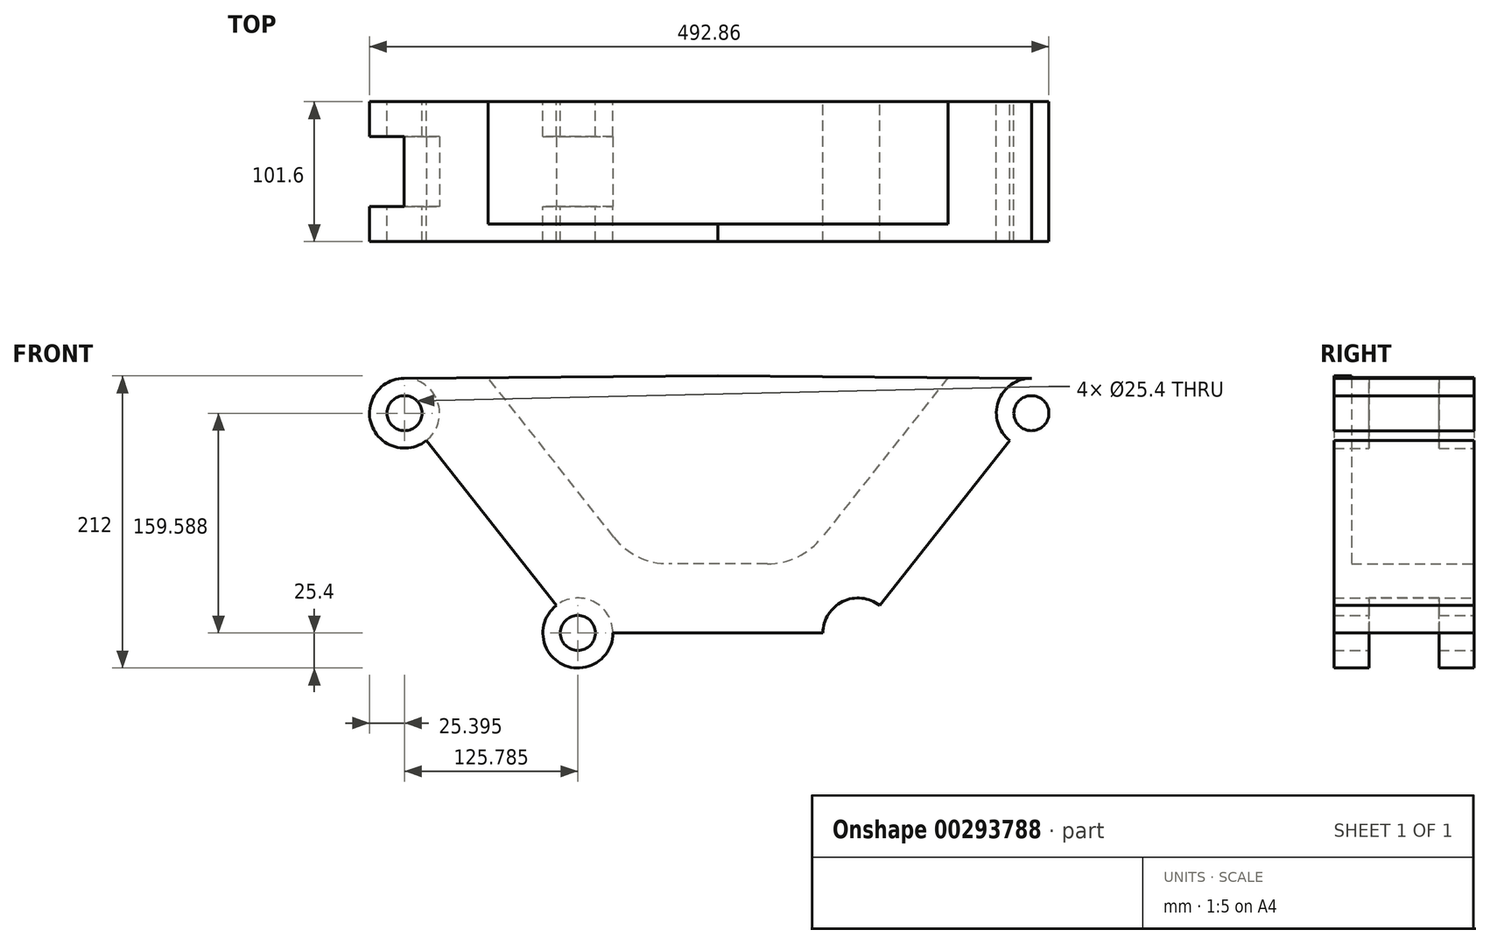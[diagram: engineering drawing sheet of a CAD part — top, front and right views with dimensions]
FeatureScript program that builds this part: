
annotation { "Feature Type Name" : "Feature", "Feature Type Description" : "" }
export const myFeature = defineFeature(function(context is Context, id is Id, definition is map)
    precondition{}
    {
        {
            var Q0;
            Q0=qCreatedBy(makeId("Front.planeOp"),FACE);
            var sketch = newSketch(context, id + "F0", { "sketchPlane" : qUnion([Q0])});
            skLineSegment(sketch, "E0", {"start": v(0, 0) * mm, "end": v(0, 76.2) * mm, "construction": true});
            skLineSegment(sketch, "E1", {"start": v(0, 0) * mm, "end": v(-101.6, 0) * mm});
            skLineSegment(sketch, "E2", {"start": v(-101.6, 0) * mm, "end": v(-227.38, 159.59) * mm});
            skCircle(sketch, "E3", {"center": v(-101.6, 0) * mm, "radius": 12.7 * mm});
            skCircle(sketch, "E4", {"center": v(-101.6, 0) * mm, "radius": 25.4 * mm});
            skCircle(sketch, "E5", {"center": v(-227.38, 159.59) * mm, "radius": 12.7 * mm});
            skCircle(sketch, "E6", {"center": v(-227.38, 159.59) * mm, "radius": 25.4 * mm});
            skLineSegment(sketch, "E7", {"start": v(-227.56, 184.99) * mm, "end": v(0, 186.6) * mm});
            skLineSegment(sketch, "E8.MirrorCS", {"start": v(227.56, 184.99) * mm, "end": v(0, 186.6) * mm});
            skCircle(sketch, "E9.MirrorC", {"center": v(227.38, 159.59) * mm, "radius": 25.4 * mm});
            skCircle(sketch, "E10.MirrorC", {"center": v(227.38, 159.59) * mm, "radius": 12.7 * mm});
            skCircle(sketch, "E11.MirrorC", {"center": v(101.6, 0) * mm, "radius": 25.4 * mm});
            skCircle(sketch, "E12.MirrorC", {"center": v(101.6, 0) * mm, "radius": 12.7 * mm});
            skLineSegment(sketch, "E13.MirrorCS", {"start": v(101.6, 0) * mm, "end": v(227.38, 159.59) * mm});
            skLineSegment(sketch, "E14.MirrorCS", {"start": v(0, 0) * mm, "end": v(101.6, 0) * mm});
            skSolve(sketch);
        }
        {
            var Q0;
            {var subQ0=sQuery(id+"F0.wireOp",EDGE,"E7");Q0=makeQuery(id+"F0.imprint","IMPRINT",FACE,{"disambiguationData":[TD([[makeQuery(id+"F0.imprint","IMPRINT",EDGE,{"derivedFrom":subQ0}),-1.0]])]});}
            cPlane(context, id + "F1", {"entities" : qUnion([Q0]), "cplaneType" : CPlaneType.OFFSET, "offset" : 101.6 * mm, "width" : 152.4 * mm, "height" : 152.4 * mm});
        }
        {
            var Q0;
            {var subQ0=sQuery(id+"F0.wireOp",EDGE,"E7");Q0=makeQuery(id+"F0.imprint","IMPRINT",FACE,{"disambiguationData":[TD([[makeQuery(id+"F0.imprint","IMPRINT",EDGE,{"derivedFrom":subQ0}),-1.0]])]});}
            var Q1;
            Q1=makeQuery(id+"F0.imprint","IMPRINT",FACE,{"disambiguationData":[TD([[makeQuery(id+"F0.imprint","IMPRINT",EDGE,{"derivedFrom":sQuery(id+"F0.wireOp",EDGE,"E5")}),-1.0]])]});
            var Q2;
            {var subQ0=sQuery(id+"F0.wireOp",EDGE,"E4");var subQ1=sQuery(id+"F0.wireOp",EDGE,"E1");var subQ2=makeQuery(id+"F0.imprint","INTERSECT",VERTEX,{"derivedFrom":[subQ1,subQ0]});Q2=makeQuery(id+"F0.imprint","IMPRINT",FACE,{"disambiguationData":[TD([[makeQuery(id+"F0.imprint","IMPRINT",EDGE,{"disambiguationData":[TD([[subQ2,-1.0]])],"derivedFrom":subQ1}),1.0]])]});}
            var Q3;
            {var subQ0=sQuery(id+"F0.wireOp",EDGE,"E13.MirrorCS");var subQ1=sQuery(id+"F0.wireOp",EDGE,"E11.MirrorC");var subQ2=makeQuery(id+"F0.imprint","INTERSECT",VERTEX,{"derivedFrom":[subQ1,subQ0]});Q3=makeQuery(id+"F0.imprint","IMPRINT",FACE,{"disambiguationData":[TD([[makeQuery(id+"F0.imprint","IMPRINT",EDGE,{"disambiguationData":[TD([[subQ2,-1.0]])],"derivedFrom":subQ1}),-1.0]])]});}
            var Q4;
            {var subQ0=sQuery(id+"F0.wireOp",EDGE,"E13.MirrorCS");var subQ1=sQuery(id+"F0.wireOp",EDGE,"E11.MirrorC");var subQ2=makeQuery(id+"F0.imprint","INTERSECT",VERTEX,{"derivedFrom":[subQ1,subQ0]});Q4=makeQuery(id+"F0.imprint","IMPRINT",FACE,{"disambiguationData":[TD([[makeQuery(id+"F0.imprint","IMPRINT",EDGE,{"disambiguationData":[TD([[subQ2,1.0]])],"derivedFrom":subQ1}),-1.0]])]});}
            var Q5;
            {var subQ0=sQuery(id+"F0.wireOp",EDGE,"E4");var subQ1=sQuery(id+"F0.wireOp",EDGE,"E1");var subQ2=makeQuery(id+"F0.imprint","INTERSECT",VERTEX,{"derivedFrom":[subQ1,subQ0]});Q5=makeQuery(id+"F0.imprint","IMPRINT",FACE,{"disambiguationData":[TD([[makeQuery(id+"F0.imprint","IMPRINT",EDGE,{"disambiguationData":[TD([[subQ2,-1.0]])],"derivedFrom":subQ1}),-1.0]])]});}
            var Q6;
            Q6=makeQuery(id+"F0.imprint","IMPRINT",FACE,{"disambiguationData":[TD([[makeQuery(id+"F0.imprint","IMPRINT",EDGE,{"derivedFrom":sQuery(id+"F0.wireOp",EDGE,"E10.MirrorC")}),1.0]])]});
            var Q7;
            Q7=qCreatedBy(id+"F1.planeOp",FACE);
            extrude(context, id + "F2", {"entities" : qUnion([Q0, Q1, Q2, Q3, Q4, Q5, Q6]), "endBound" : BoundingType.SYMMETRIC, "endBoundEntityFace" : qUnion([Q7]), "depth" : 101.6 * mm});
        }
        {
            var Q0;
            Q0=makeQuery(id+"F2.opExtrude","CAP_FACE",FACE,{"disambiguationData":[OSD([sQuery(id+"F0.wireOp",EDGE,"E1"),sQuery(id+"F0.wireOp",EDGE,"E2"),sQuery(id+"F0.wireOp",EDGE,"E3"),sQuery(id+"F0.wireOp",EDGE,"E4"),sQuery(id+"F0.wireOp",EDGE,"E5"),sQuery(id+"F0.wireOp",EDGE,"E6"),sQuery(id+"F0.wireOp",EDGE,"E7"),sQuery(id+"F0.wireOp",EDGE,"E8.MirrorCS"),sQuery(id+"F0.wireOp",EDGE,"E9.MirrorC"),sQuery(id+"F0.wireOp",EDGE,"E10.MirrorC"),sQuery(id+"F0.wireOp",EDGE,"E11.MirrorC"),sQuery(id+"F0.wireOp",EDGE,"E12.MirrorC"),sQuery(id+"F0.wireOp",EDGE,"E13.MirrorCS"),sQuery(id+"F0.wireOp",EDGE,"E14.MirrorCS")])],"isStart":true});
            var sketch = newSketch(context, id + "F3", { "sketchPlane" : qUnion([Q0])});
            skLineSegment(sketch, "E15", {"start": v(-166.9, 185.42) * mm, "end": v(-60.34, 50.23) * mm});
            skLineSegment(sketch, "E16", {"start": v(-60.34, 50.23) * mm, "end": v(60.34, 50.23) * mm});
            skLineSegment(sketch, "E17", {"start": v(60.34, 50.23) * mm, "end": v(166.9, 185.42) * mm});
            skSolve(sketch);
        }
        {
            var Q0;
            {var subQ4=sQuery(id+"F3.wireOp",EDGE,"E15");Q0=makeQuery(id+"F3.imprint","IMPRINT",FACE,{"disambiguationData":[TD([[makeQuery(id+"F3.imprint","IMPRINT",EDGE,{"derivedFrom":subQ4}),1.0]])]});}
            extrude(context, id + "F4", {"entities" : qUnion([Q0]), "operationType" : NewBodyOperationType.REMOVE, "oppositeDirection" : true, "depth" : 88.9 * mm});
        }
        {
            var Q0;
            Q0=makeQuery(id+"F4.boolean.opBoolean","COPY",EDGE,{"derivedFrom":makeQuery(id+"F4.opExtrude","SWEPT_EDGE",EDGE,{"disambiguationData":[OSD([sQuery(id+"F0.wireOp",EDGE,"E8.MirrorCS"),sQuery(id+"F3.wireOp",EDGE,"E15")])]})});
            var Q1;
            Q1=makeQuery(id+"F4.boolean.opBoolean","COPY",EDGE,{"derivedFrom":makeQuery(id+"F4.opExtrude","SWEPT_EDGE",EDGE,{"disambiguationData":[OSD([sQuery(id+"F0.wireOp",EDGE,"E7"),sQuery(id+"F3.wireOp",EDGE,"E17")])]})});
            var Q2;
            Q2=makeQuery(id+"F4.boolean.opBoolean","COPY",EDGE,{"derivedFrom":makeQuery(id+"F4.opExtrude","SWEPT_EDGE",EDGE,{"disambiguationData":[OSD([sQuery(id+"F3.wireOp",EDGE,"E16"),sQuery(id+"F3.wireOp",EDGE,"E17")])]})});
            var Q3;
            Q3=makeQuery(id+"F4.boolean.opBoolean","COPY",EDGE,{"derivedFrom":makeQuery(id+"F4.opExtrude","SWEPT_EDGE",EDGE,{"disambiguationData":[OSD([sQuery(id+"F3.wireOp",EDGE,"E15"),sQuery(id+"F3.wireOp",EDGE,"E16")])]})});
            fillet(context, id + "F5", {"entities" : qUnion([Q0, Q1, Q2, Q3]), "radius" : 50.8 * mm, "tangentPropagation" : true, "allowEdgeOverflow" : false});
        }
        {
            var Q0;
            {var subQ0=sQuery(id+"F0.wireOp",EDGE,"E7");Q0=makeQuery(id+"F0.imprint","IMPRINT",FACE,{"disambiguationData":[TD([[makeQuery(id+"F0.imprint","IMPRINT",EDGE,{"derivedFrom":subQ0}),-1.0]])]});}
            var sketch = newSketch(context, id + "F6", { "sketchPlane" : qUnion([Q0])});
            skCircle(sketch, "E18.0", {"center": v(227.38, 159.59) * mm, "radius": 12.7 * mm});
            skCircle(sketch, "E19.0", {"center": v(101.6, 0) * mm, "radius": 12.7 * mm});
            skCircle(sketch, "E20.0", {"center": v(-101.6, 0) * mm, "radius": 12.7 * mm});
            skCircle(sketch, "E21.0", {"center": v(-227.38, 159.59) * mm, "radius": 12.7 * mm});
            skCircle(sketch, "E22", {"center": v(227.38, 159.59) * mm, "radius": 33.02 * mm});
            skCircle(sketch, "E23", {"center": v(101.6, 0) * mm, "radius": 33.02 * mm});
            skCircle(sketch, "E24", {"center": v(-101.6, 0) * mm, "radius": 33.02 * mm});
            skCircle(sketch, "E25", {"center": v(-227.38, 159.59) * mm, "radius": 33.02 * mm});
            skSolve(sketch);
        }
        {
            var Q0;
            Q0=makeQuery(id+"F6.imprint","IMPRINT",FACE,{"disambiguationData":[TD([[makeQuery(id+"F6.imprint","IMPRINT",EDGE,{"derivedFrom":sQuery(id+"F6.wireOp",EDGE,"E18.0")}),-1.0]])]});
            var Q1;
            Q1=makeQuery(id+"F6.imprint","IMPRINT",FACE,{"disambiguationData":[TD([[makeQuery(id+"F6.imprint","IMPRINT",EDGE,{"derivedFrom":sQuery(id+"F6.wireOp",EDGE,"E19.0")}),-1.0]])]});
            var Q2;
            Q2=makeQuery(id+"F6.imprint","IMPRINT",FACE,{"disambiguationData":[TD([[makeQuery(id+"F6.imprint","IMPRINT",EDGE,{"derivedFrom":sQuery(id+"F6.wireOp",EDGE,"E20.0")}),-1.0]])]});
            var Q3;
            Q3=makeQuery(id+"F6.imprint","IMPRINT",FACE,{"disambiguationData":[TD([[makeQuery(id+"F6.imprint","IMPRINT",EDGE,{"derivedFrom":sQuery(id+"F6.wireOp",EDGE,"E21.0")}),-1.0]])]});
            extrude(context, id + "F7", {"entities" : qUnion([Q0, Q1, Q2, Q3]), "operationType" : NewBodyOperationType.REMOVE, "endBound" : BoundingType.SYMMETRIC, "oppositeDirection" : true, "depth" : 50.8 * mm});
        }
    });
